# Revit family: SF_Tubest
name_source: partatom
category: Structural Framing
units: mm (PartAtom-declared; Revit-internal decimal feet)

## family parameters
Always export as geometry = No
Always vertical = Yes
Cut with Voids When Loaded = No
Material for Model Behavior = Other
OmniClass Number = 23.25.30.11.14.14
OmniClass Title = Beams
Section Shape = Not Defined
Shared = No
Show family pre-cut in plan views = Yes

## types (264) — shared parameters
A = 89 mm
D2_o = 18 mm
D2_s = 20 mm
D_o = 18 mm
D_s = 25 mm
Dse = 20 mm
Ro = 10 mm
Rs = 8 mm

## per-type parameters (varying)
| type | B | H | Offset_o | Offset_s | Vis.Sigma | Vis.SigmaEspecial | Y | eo | es |
| TubestGD (800x400x6x4 | 400 mm | 800 mm | 400 mm | 200 mm | Yes | No | 670 mm | 6 mm | 4 mm |
| TubestGD (800x400x6x3 | 400 mm | 800 mm | 400 mm | 200 mm | Yes | No | 670 mm | 6 mm | 3 mm |
| TubestGD (800x400x5x3 | 400 mm | 800 mm | 400 mm | 200 mm | Yes | No | 670 mm | 5 mm | 3 mm |
| TubestGD (800x400x4x3 | 400 mm | 800 mm | 400 mm | 200 mm | Yes | No | 670 mm | 4 mm | 3 mm |
| TubestGD (800x400x3x3 | 400 mm | 800 mm | 400 mm | 200 mm | Yes | No | 670 mm | 3 mm | 3 mm |
| TubestGD (800x350x6x4 | 350 mm | 800 mm | 400 mm | 175 mm | Yes | No | 670 mm | 6 mm | 4 mm |
| TubestGD (800x350x6x3 | 350 mm | 800 mm | 400 mm | 175 mm | Yes | No | 670 mm | 6 mm | 3 mm |
| TubestGD (800x350x5x3 | 350 mm | 800 mm | 400 mm | 175 mm | Yes | No | 670 mm | 5 mm | 3 mm |
| TubestGD (800x350x4x3 | 350 mm | 800 mm | 400 mm | 175 mm | Yes | No | 670 mm | 4 mm | 3 mm |
| TubestGD (800x350x3x3 | 350 mm | 800 mm | 400 mm | 175 mm | Yes | No | 670 mm | 3 mm | 3 mm |
| TubestGD (800x300x6x4 | 300 mm | 800 mm | 400 mm | 150 mm | Yes | No | 670 mm | 6 mm | 4 mm |
| TubestGD (800x300x6x3 | 300 mm | 800 mm | 400 mm | 150 mm | Yes | No | 670 mm | 6 mm | 3 mm |
| TubestGD (800x300x5x3 | 300 mm | 800 mm | 400 mm | 150 mm | Yes | No | 670 mm | 5 mm | 3 mm |
| TubestGD (800x300x4x3 | 300 mm | 800 mm | 400 mm | 150 mm | Yes | No | 670 mm | 4 mm | 3 mm |
| TubestGD (800x300x3x3 | 300 mm | 800 mm | 400 mm | 150 mm | Yes | No | 670 mm | 3 mm | 3 mm |
| TubestGD (800x250x6x4 | 250 mm | 800 mm | 400 mm | 125 mm | Yes | No | 670 mm | 6 mm | 4 mm |
| TubestGD (800x250x6x3 | 250 mm | 800 mm | 400 mm | 125 mm | Yes | No | 670 mm | 6 mm | 3 mm |
| TubestGD (800x250x5x3 | 250 mm | 800 mm | 400 mm | 125 mm | Yes | No | 670 mm | 5 mm | 3 mm |
| TubestGD (800x250x4x3 | 250 mm | 800 mm | 400 mm | 125 mm | Yes | No | 670 mm | 4 mm | 3 mm |
| TubestGD (800x250x3x3 | 250 mm | 800 mm | 400 mm | 125 mm | Yes | No | 670 mm | 3 mm | 3 mm |
| TubestGD (800x225x6x4 | 225 mm | 800 mm | 400 mm | 113 mm | Yes | No | 670 mm | 6 mm | 4 mm |
| TubestGD (800x225x6x3 | 225 mm | 800 mm | 400 mm | 113 mm | Yes | No | 670 mm | 6 mm | 3 mm |
| TubestGD (800x225x5x3 | 225 mm | 800 mm | 400 mm | 113 mm | Yes | No | 670 mm | 5 mm | 3 mm |
| TubestGD (800x225x4x3 | 225 mm | 800 mm | 400 mm | 113 mm | Yes | No | 670 mm | 4 mm | 3 mm |
| TubestGD (800x225x3x3 | 225 mm | 800 mm | 400 mm | 113 mm | Yes | No | 670 mm | 3 mm | 3 mm |
| TubestGD (800x200x6x4 | 200 mm | 800 mm | 400 mm | 100 mm | Yes | No | 670 mm | 6 mm | 4 mm |
| TubestGD (800x200x6x3 | 200 mm | 800 mm | 400 mm | 100 mm | Yes | No | 670 mm | 6 mm | 3 mm |
| TubestGD (800x200x5x3 | 200 mm | 800 mm | 400 mm | 100 mm | Yes | No | 670 mm | 5 mm | 3 mm |
| TubestGD (800x200x4x3 | 200 mm | 800 mm | 400 mm | 100 mm | Yes | No | 670 mm | 4 mm | 3 mm |
| TubestGD (800x200x3x3 | 200 mm | 800 mm | 400 mm | 100 mm | Yes | No | 670 mm | 3 mm | 3 mm |
| TubestGD (800x150x6x4 | 150 mm | 800 mm | 400 mm | 75 mm | Yes | No | 670 mm | 6 mm | 4 mm |
| TubestGD (800x150x6x3 | 150 mm | 800 mm | 400 mm | 75 mm | Yes | No | 670 mm | 6 mm | 3 mm |
| TubestGD (800x150x5x3 | 150 mm | 800 mm | 400 mm | 75 mm | Yes | No | 670 mm | 5 mm | 3 mm |
| TubestGD (800x150x4x3 | 150 mm | 800 mm | 400 mm | 75 mm | Yes | No | 670 mm | 4 mm | 3 mm |
| TubestGD (800x150x3x3 | 150 mm | 800 mm | 400 mm | 75 mm | Yes | No | 670 mm | 3 mm | 3 mm |
| TubestGD (750x400x6x4 | 400 mm | 750 mm | 375 mm | 200 mm | Yes | No | 620 mm | 6 mm | 4 mm |
| TubestGD (750x400x6x3 | 400 mm | 750 mm | 375 mm | 200 mm | Yes | No | 620 mm | 6 mm | 3 mm |
| TubestGD (750x400x5x3 | 400 mm | 750 mm | 375 mm | 200 mm | Yes | No | 620 mm | 5 mm | 3 mm |
| TubestGD (750x400x4x3 | 400 mm | 750 mm | 375 mm | 200 mm | Yes | No | 620 mm | 4 mm | 3 mm |
| TubestGD (750x400x3x3 | 400 mm | 750 mm | 375 mm | 200 mm | Yes | No | 620 mm | 3 mm | 3 mm |
| TubestGD (750x350x6x4 | 350 mm | 750 mm | 375 mm | 175 mm | Yes | No | 620 mm | 6 mm | 4 mm |
| TubestGD (750x350x6x3 | 350 mm | 750 mm | 375 mm | 175 mm | Yes | No | 620 mm | 6 mm | 3 mm |
| TubestGD (750x350x5x3 | 350 mm | 750 mm | 375 mm | 175 mm | Yes | No | 620 mm | 5 mm | 3 mm |
| TubestGD (750x350x4x3 | 350 mm | 750 mm | 375 mm | 175 mm | Yes | No | 620 mm | 4 mm | 3 mm |
| TubestGD (750x350x3x3 | 350 mm | 750 mm | 375 mm | 175 mm | Yes | No | 620 mm | 3 mm | 3 mm |
| TubestGD (750x300x6x4 | 300 mm | 750 mm | 375 mm | 150 mm | Yes | No | 620 mm | 6 mm | 4 mm |
| TubestGD (750x300x6x3 | 300 mm | 750 mm | 375 mm | 150 mm | Yes | No | 620 mm | 6 mm | 3 mm |
| TubestGD (750x300x5x3 | 300 mm | 750 mm | 375 mm | 150 mm | Yes | No | 620 mm | 5 mm | 3 mm |
| TubestGD (750x300x4x3 | 300 mm | 750 mm | 375 mm | 150 mm | Yes | No | 620 mm | 4 mm | 3 mm |
| TubestGD (750x300x3x3 | 300 mm | 750 mm | 375 mm | 150 mm | Yes | No | 620 mm | 3 mm | 3 mm |
| TubestGD (750x250x6x4 | 250 mm | 750 mm | 375 mm | 125 mm | Yes | No | 620 mm | 6 mm | 4 mm |
| TubestGD (750x250x6x3 | 250 mm | 750 mm | 375 mm | 125 mm | Yes | No | 620 mm | 6 mm | 3 mm |
| TubestGD (750x250x5x3 | 250 mm | 750 mm | 375 mm | 125 mm | Yes | No | 620 mm | 5 mm | 3 mm |
| TubestGD (750x250x4x3 | 250 mm | 750 mm | 375 mm | 125 mm | Yes | No | 620 mm | 4 mm | 3 mm |
| TubestGD (750x250x3x3 | 250 mm | 750 mm | 375 mm | 125 mm | Yes | No | 620 mm | 3 mm | 3 mm |
| TubestGD (750x225x6x4 | 225 mm | 750 mm | 375 mm | 113 mm | Yes | No | 620 mm | 6 mm | 4 mm |
| TubestGD (750x225x6x3 | 225 mm | 750 mm | 375 mm | 113 mm | Yes | No | 620 mm | 6 mm | 3 mm |
| TubestGD (750x225x5x3 | 225 mm | 750 mm | 375 mm | 113 mm | Yes | No | 620 mm | 5 mm | 3 mm |
| TubestGD (750x225x4x3 | 225 mm | 750 mm | 375 mm | 113 mm | Yes | No | 620 mm | 4 mm | 3 mm |
| TubestGD (750x225x3x3 | 225 mm | 750 mm | 375 mm | 113 mm | Yes | No | 620 mm | 3 mm | 3 mm |
| TubestGD (750x200x6x4 | 200 mm | 750 mm | 375 mm | 100 mm | Yes | No | 620 mm | 6 mm | 4 mm |
| TubestGD (750x200x6x3 | 200 mm | 750 mm | 375 mm | 100 mm | Yes | No | 620 mm | 6 mm | 3 mm |
| TubestGD (750x200x5x3 | 200 mm | 750 mm | 375 mm | 100 mm | Yes | No | 620 mm | 5 mm | 3 mm |
| TubestGD (750x200x4x3 | 200 mm | 750 mm | 375 mm | 100 mm | Yes | No | 620 mm | 4 mm | 3 mm |
| TubestGD (750x200x3x3 | 200 mm | 750 mm | 375 mm | 100 mm | Yes | No | 620 mm | 3 mm | 3 mm |
| TubestGD (750x150x6x4 | 150 mm | 750 mm | 375 mm | 75 mm | Yes | No | 620 mm | 6 mm | 4 mm |
| TubestGD (750x150x6x3 | 150 mm | 750 mm | 375 mm | 75 mm | Yes | No | 620 mm | 6 mm | 3 mm |
| TubestGD (750x150x5x3 | 150 mm | 750 mm | 375 mm | 75 mm | Yes | No | 620 mm | 5 mm | 3 mm |
| TubestGD (750x150x4x3 | 150 mm | 750 mm | 375 mm | 75 mm | Yes | No | 620 mm | 4 mm | 3 mm |
| TubestGD (750x150x3x3 | 150 mm | 750 mm | 375 mm | 75 mm | Yes | No | 620 mm | 3 mm | 3 mm |
| TubestGD (700x400x6x4 | 400 mm | 700 mm | 350 mm | 200 mm | Yes | No | 570 mm | 6 mm | 4 mm |
| TubestGD (700x400x6x3 | 400 mm | 700 mm | 350 mm | 200 mm | Yes | No | 570 mm | 6 mm | 3 mm |
| TubestGD (700x400x5x3 | 400 mm | 700 mm | 350 mm | 200 mm | Yes | No | 570 mm | 5 mm | 3 mm |
| TubestGD (700x400x4x3 | 400 mm | 700 mm | 350 mm | 200 mm | Yes | No | 570 mm | 4 mm | 3 mm |
| TubestGD (700x400x3x3 | 400 mm | 700 mm | 350 mm | 200 mm | Yes | No | 570 mm | 3 mm | 3 mm |
| TubestGD (700x350x6x4 | 350 mm | 700 mm | 350 mm | 175 mm | Yes | No | 570 mm | 6 mm | 4 mm |
| TubestGD (700x350x6x3 | 350 mm | 700 mm | 350 mm | 175 mm | Yes | No | 570 mm | 6 mm | 3 mm |
| TubestGD (700x350x5x3 | 350 mm | 700 mm | 350 mm | 175 mm | Yes | No | 570 mm | 5 mm | 3 mm |
| TubestGD (700x350x4x3 | 350 mm | 700 mm | 350 mm | 175 mm | Yes | No | 570 mm | 4 mm | 3 mm |
| TubestGD (700x350x3x3 | 350 mm | 700 mm | 350 mm | 175 mm | Yes | No | 570 mm | 3 mm | 3 mm |
| TubestGD (700x300x6x4 | 300 mm | 700 mm | 350 mm | 150 mm | Yes | No | 570 mm | 6 mm | 4 mm |
| TubestGD (700x300x6x3 | 300 mm | 700 mm | 350 mm | 150 mm | Yes | No | 570 mm | 6 mm | 3 mm |
| TubestGD (700x300x5x3 | 300 mm | 700 mm | 350 mm | 150 mm | Yes | No | 570 mm | 5 mm | 3 mm |
| TubestGD (700x300x4x3 | 300 mm | 700 mm | 350 mm | 150 mm | Yes | No | 570 mm | 4 mm | 3 mm |
| TubestGD (700x300x3x3 | 300 mm | 700 mm | 350 mm | 150 mm | Yes | No | 570 mm | 3 mm | 3 mm |
| TubestGD (700x250x6x4 | 250 mm | 700 mm | 350 mm | 125 mm | Yes | No | 570 mm | 6 mm | 4 mm |
| TubestGD (700x250x6x3 | 250 mm | 700 mm | 350 mm | 125 mm | Yes | No | 570 mm | 6 mm | 3 mm |
| TubestGD (700x250x5x3 | 250 mm | 700 mm | 350 mm | 125 mm | Yes | No | 570 mm | 5 mm | 3 mm |
| TubestGD (700x250x4x3 | 250 mm | 700 mm | 350 mm | 125 mm | Yes | No | 570 mm | 4 mm | 3 mm |
| TubestGD (700x250x3x3 | 250 mm | 700 mm | 350 mm | 125 mm | Yes | No | 570 mm | 3 mm | 3 mm |
| TubestGD (700x225x6x4 | 225 mm | 700 mm | 350 mm | 113 mm | Yes | No | 570 mm | 6 mm | 4 mm |
| TubestGD (700x225x6x3 | 225 mm | 700 mm | 350 mm | 113 mm | Yes | No | 570 mm | 6 mm | 3 mm |
| TubestGD (700x225x5x3 | 225 mm | 700 mm | 350 mm | 113 mm | Yes | No | 570 mm | 5 mm | 3 mm |
| TubestGD (700x225x4x3 | 225 mm | 700 mm | 350 mm | 113 mm | Yes | No | 570 mm | 4 mm | 3 mm |
| TubestGD (700x225x3x3 | 225 mm | 700 mm | 350 mm | 113 mm | Yes | No | 570 mm | 3 mm | 3 mm |
| TubestGD (700x200x6x4 | 200 mm | 700 mm | 350 mm | 100 mm | Yes | No | 570 mm | 6 mm | 4 mm |
| TubestGD (700x200x6x3 | 200 mm | 700 mm | 350 mm | 100 mm | Yes | No | 570 mm | 6 mm | 3 mm |
| TubestGD (700x200x5x3 | 200 mm | 700 mm | 350 mm | 100 mm | Yes | No | 570 mm | 5 mm | 3 mm |
| TubestGD (700x200x4x3 | 200 mm | 700 mm | 350 mm | 100 mm | Yes | No | 570 mm | 4 mm | 3 mm |
| TubestGD (700x200x3x3 | 200 mm | 700 mm | 350 mm | 100 mm | Yes | No | 570 mm | 3 mm | 3 mm |
| TubestGD (700x150x6x4 | 150 mm | 700 mm | 350 mm | 75 mm | Yes | No | 570 mm | 6 mm | 4 mm |
| TubestGD (700x150x6x3 | 150 mm | 700 mm | 350 mm | 75 mm | Yes | No | 570 mm | 6 mm | 3 mm |
| TubestGD (700x150x5x3 | 150 mm | 700 mm | 350 mm | 75 mm | Yes | No | 570 mm | 5 mm | 3 mm |
| TubestGD (700x150x4x3 | 150 mm | 700 mm | 350 mm | 75 mm | Yes | No | 570 mm | 4 mm | 3 mm |
| TubestGD (700x150x3x3 | 150 mm | 700 mm | 350 mm | 75 mm | Yes | No | 570 mm | 3 mm | 3 mm |
| TubestGD (650x400x6x4 | 400 mm | 650 mm | 325 mm | 200 mm | Yes | No | 520 mm | 6 mm | 4 mm |
| TubestGD (650x400x6x3 | 400 mm | 650 mm | 325 mm | 200 mm | Yes | No | 520 mm | 6 mm | 3 mm |
| TubestGD (650x400x5x3 | 400 mm | 650 mm | 325 mm | 200 mm | Yes | No | 520 mm | 5 mm | 3 mm |
| TubestGD (650x400x4x3 | 400 mm | 650 mm | 325 mm | 200 mm | Yes | No | 520 mm | 4 mm | 3 mm |
| TubestGD (650x400x3x3 | 400 mm | 650 mm | 325 mm | 200 mm | Yes | No | 520 mm | 3 mm | 3 mm |
| TubestGD (650x350x6x4 | 350 mm | 650 mm | 325 mm | 175 mm | Yes | No | 520 mm | 6 mm | 4 mm |
| TubestGD (650x350x6x3 | 350 mm | 650 mm | 325 mm | 175 mm | Yes | No | 520 mm | 6 mm | 3 mm |
| TubestGD (650x350x5x3 | 350 mm | 650 mm | 325 mm | 175 mm | Yes | No | 520 mm | 5 mm | 3 mm |
| TubestGD (650x350x4x3 | 350 mm | 650 mm | 325 mm | 175 mm | Yes | No | 520 mm | 4 mm | 3 mm |
| TubestGD (650x350x3x3 | 350 mm | 650 mm | 325 mm | 175 mm | Yes | No | 520 mm | 3 mm | 3 mm |
| TubestGD (650x300x6x4 | 300 mm | 650 mm | 325 mm | 150 mm | Yes | No | 520 mm | 6 mm | 4 mm |
| TubestGD (650x300x6x3 | 300 mm | 650 mm | 325 mm | 150 mm | Yes | No | 520 mm | 6 mm | 3 mm |
| TubestGD (650x300x5x3 | 300 mm | 650 mm | 325 mm | 150 mm | Yes | No | 520 mm | 5 mm | 3 mm |
| TubestGD (650x300x4x3 | 300 mm | 650 mm | 325 mm | 150 mm | Yes | No | 520 mm | 4 mm | 3 mm |
| TubestGD (650x300x3x3 | 300 mm | 650 mm | 325 mm | 150 mm | Yes | No | 520 mm | 3 mm | 3 mm |
| TubestGD (650x250x6x4 | 250 mm | 650 mm | 325 mm | 125 mm | Yes | No | 520 mm | 6 mm | 4 mm |
| TubestGD (650x250x6x3 | 250 mm | 650 mm | 325 mm | 125 mm | Yes | No | 520 mm | 6 mm | 3 mm |
| TubestGD (650x250x5x3 | 250 mm | 650 mm | 325 mm | 125 mm | Yes | No | 520 mm | 5 mm | 3 mm |
| TubestGD (650x250x4x3 | 250 mm | 650 mm | 325 mm | 125 mm | Yes | No | 520 mm | 4 mm | 3 mm |
| TubestGD (650x250x3x3 | 250 mm | 650 mm | 325 mm | 125 mm | Yes | No | 520 mm | 3 mm | 3 mm |
| TubestGD (650x225x6x4 | 225 mm | 650 mm | 325 mm | 113 mm | Yes | No | 520 mm | 6 mm | 4 mm |
| TubestGD (650x225x6x3 | 225 mm | 650 mm | 325 mm | 113 mm | Yes | No | 520 mm | 6 mm | 3 mm |
| TubestGD (650x225x5x3 | 225 mm | 650 mm | 325 mm | 113 mm | Yes | No | 520 mm | 5 mm | 3 mm |
| TubestGD (650x225x4x3 | 225 mm | 650 mm | 325 mm | 113 mm | Yes | No | 520 mm | 4 mm | 3 mm |
| TubestGD (650x225x3x3 | 225 mm | 650 mm | 325 mm | 113 mm | Yes | No | 520 mm | 3 mm | 3 mm |
| TubestGD (650x200x6x4 | 200 mm | 650 mm | 325 mm | 100 mm | Yes | No | 520 mm | 6 mm | 4 mm |
| TubestGD (650x200x6x3 | 200 mm | 650 mm | 325 mm | 100 mm | Yes | No | 520 mm | 6 mm | 3 mm |
| TubestGD (650x200x5x3 | 200 mm | 650 mm | 325 mm | 100 mm | Yes | No | 520 mm | 5 mm | 3 mm |
| TubestGD (650x200x4x3 | 200 mm | 650 mm | 325 mm | 100 mm | Yes | No | 520 mm | 4 mm | 3 mm |
| TubestGD (650x200x3x3 | 200 mm | 650 mm | 325 mm | 100 mm | Yes | No | 520 mm | 3 mm | 3 mm |
| TubestGD (650x150x6x4 | 150 mm | 650 mm | 325 mm | 75 mm | Yes | No | 520 mm | 6 mm | 4 mm |
| TubestGD (650x150x6x3 | 150 mm | 650 mm | 325 mm | 75 mm | Yes | No | 520 mm | 6 mm | 3 mm |
| TubestGD (650x150x5x3 | 150 mm | 650 mm | 325 mm | 75 mm | Yes | No | 520 mm | 5 mm | 3 mm |
| TubestGD (650x150x4x3 | 150 mm | 650 mm | 325 mm | 75 mm | Yes | No | 520 mm | 4 mm | 3 mm |
| TubestGD (650x150x3x3 | 150 mm | 650 mm | 325 mm | 75 mm | Yes | No | 520 mm | 3 mm | 3 mm |
| TubestGD (600x400x6x4 | 400 mm | 600 mm | 300 mm | 200 mm | Yes | No | 470 mm | 6 mm | 4 mm |
| TubestGD (600x400x6x3 | 400 mm | 600 mm | 300 mm | 200 mm | Yes | No | 470 mm | 6 mm | 3 mm |
| TubestGD (600x400x5x3 | 400 mm | 600 mm | 300 mm | 200 mm | Yes | No | 470 mm | 5 mm | 3 mm |
| TubestGD (600x400x4x3 | 400 mm | 600 mm | 300 mm | 200 mm | Yes | No | 470 mm | 4 mm | 3 mm |
| TubestGD (600x400x3x3 | 400 mm | 600 mm | 300 mm | 200 mm | Yes | No | 470 mm | 3 mm | 3 mm |
| TubestGD (600x350x6x4 | 350 mm | 600 mm | 300 mm | 175 mm | Yes | No | 470 mm | 6 mm | 4 mm |
| TubestGD (600x350x6x3 | 350 mm | 600 mm | 300 mm | 175 mm | Yes | No | 470 mm | 6 mm | 3 mm |
| TubestGD (600x350x5x3 | 350 mm | 600 mm | 300 mm | 175 mm | Yes | No | 470 mm | 5 mm | 3 mm |
| TubestGD (600x350x4x3 | 350 mm | 600 mm | 300 mm | 175 mm | Yes | No | 470 mm | 4 mm | 3 mm |
| TubestGD (600x350x3x3 | 350 mm | 600 mm | 300 mm | 175 mm | Yes | No | 470 mm | 3 mm | 3 mm |
| TubestGD (600x300x6x4 | 300 mm | 600 mm | 300 mm | 150 mm | Yes | No | 470 mm | 6 mm | 4 mm |
| TubestGD (600x300x6x3 | 300 mm | 600 mm | 300 mm | 150 mm | Yes | No | 470 mm | 6 mm | 3 mm |
| TubestGD (600x300x5x3 | 300 mm | 600 mm | 300 mm | 150 mm | Yes | No | 470 mm | 5 mm | 3 mm |
| TubestGD (600x300x4x3 | 300 mm | 600 mm | 300 mm | 150 mm | Yes | No | 470 mm | 4 mm | 3 mm |
| TubestGD (600x300x3x3 | 300 mm | 600 mm | 300 mm | 150 mm | Yes | No | 470 mm | 3 mm | 3 mm |
| TubestGD (600x250x6x4 | 250 mm | 600 mm | 300 mm | 125 mm | Yes | No | 470 mm | 6 mm | 4 mm |
| TubestGD (600x250x6x3 | 250 mm | 600 mm | 300 mm | 125 mm | Yes | No | 470 mm | 6 mm | 3 mm |
| TubestGD (600x250x5x3 | 250 mm | 600 mm | 300 mm | 125 mm | Yes | No | 470 mm | 5 mm | 3 mm |
| TubestGD (600x250x4x3 | 250 mm | 600 mm | 300 mm | 125 mm | Yes | No | 470 mm | 4 mm | 3 mm |
| TubestGD (600x250x3x3 | 250 mm | 600 mm | 300 mm | 125 mm | Yes | No | 470 mm | 3 mm | 3 mm |
| TubestGD (600x225x6x4 | 225 mm | 600 mm | 300 mm | 113 mm | Yes | No | 470 mm | 6 mm | 4 mm |
| TubestGD (600x225x6x3 | 225 mm | 600 mm | 300 mm | 113 mm | Yes | No | 470 mm | 6 mm | 3 mm |
| TubestGD (600x225x5x3 | 225 mm | 600 mm | 300 mm | 113 mm | Yes | No | 470 mm | 5 mm | 3 mm |
| TubestGD (600x225x4x3 | 225 mm | 600 mm | 300 mm | 113 mm | Yes | No | 470 mm | 4 mm | 3 mm |
| TubestGD (600x225x3x3 | 225 mm | 600 mm | 300 mm | 113 mm | Yes | No | 470 mm | 3 mm | 3 mm |
| TubestGD (600x200x6x4 | 200 mm | 600 mm | 300 mm | 100 mm | Yes | No | 470 mm | 6 mm | 4 mm |
| TubestGD (600x200x6x3 | 200 mm | 600 mm | 300 mm | 100 mm | Yes | No | 470 mm | 6 mm | 3 mm |
| TubestGD (600x200x5x3 | 200 mm | 600 mm | 300 mm | 100 mm | Yes | No | 470 mm | 5 mm | 3 mm |
| TubestGD (600x200x4x3 | 200 mm | 600 mm | 300 mm | 100 mm | Yes | No | 470 mm | 4 mm | 3 mm |
| TubestGD (600x200x3x3 | 200 mm | 600 mm | 300 mm | 100 mm | Yes | No | 470 mm | 3 mm | 3 mm |
| TubestGD (600x150x6x4 | 150 mm | 600 mm | 300 mm | 75 mm | Yes | No | 470 mm | 6 mm | 4 mm |
| TubestGD (600x150x6x3 | 150 mm | 600 mm | 300 mm | 75 mm | Yes | No | 470 mm | 6 mm | 3 mm |
| TubestGD (600x150x5x3 | 150 mm | 600 mm | 300 mm | 75 mm | Yes | No | 470 mm | 5 mm | 3 mm |
| TubestGD (600x150x4x3 | 150 mm | 600 mm | 300 mm | 75 mm | Yes | No | 470 mm | 4 mm | 3 mm |
| TubestGD (600x150x3x3 | 150 mm | 600 mm | 300 mm | 75 mm | Yes | No | 470 mm | 3 mm | 3 mm |
| TubestGD (550x400x6x4 | 400 mm | 550 mm | 275 mm | 200 mm | Yes | No | 420 mm | 6 mm | 4 mm |
| TubestGD (550x400x6x3 | 400 mm | 550 mm | 275 mm | 200 mm | Yes | No | 420 mm | 6 mm | 3 mm |
| TubestGD (550x400x5x3 | 400 mm | 550 mm | 275 mm | 200 mm | Yes | No | 420 mm | 5 mm | 3 mm |
| TubestGD (550x400x4x3 | 400 mm | 550 mm | 275 mm | 200 mm | Yes | No | 420 mm | 4 mm | 3 mm |
| TubestGD (550x400x3x3 | 400 mm | 550 mm | 275 mm | 200 mm | Yes | No | 420 mm | 3 mm | 3 mm |
| TubestGD (550x350x6x4 | 350 mm | 550 mm | 275 mm | 175 mm | Yes | No | 420 mm | 6 mm | 4 mm |
| TubestGD (550x350x6x3 | 350 mm | 550 mm | 275 mm | 175 mm | Yes | No | 420 mm | 6 mm | 3 mm |
| TubestGD (550x350x5x3 | 350 mm | 550 mm | 275 mm | 175 mm | Yes | No | 420 mm | 5 mm | 3 mm |
| TubestGD (550x350x4x3 | 350 mm | 550 mm | 275 mm | 175 mm | Yes | No | 420 mm | 4 mm | 3 mm |
| TubestGD (550x350x3x3 | 350 mm | 550 mm | 275 mm | 175 mm | Yes | No | 420 mm | 3 mm | 3 mm |
| TubestGD (550x300x6x4 | 300 mm | 550 mm | 275 mm | 150 mm | Yes | No | 420 mm | 6 mm | 4 mm |
| TubestGD (550x300x6x3 | 300 mm | 550 mm | 275 mm | 150 mm | Yes | No | 420 mm | 6 mm | 3 mm |
| TubestGD (550x300x5x3 | 300 mm | 550 mm | 275 mm | 150 mm | Yes | No | 420 mm | 5 mm | 3 mm |
| TubestGD (550x300x4x3 | 300 mm | 550 mm | 275 mm | 150 mm | Yes | No | 420 mm | 4 mm | 3 mm |
| TubestGD (550x300x3x3 | 300 mm | 550 mm | 275 mm | 150 mm | Yes | No | 420 mm | 3 mm | 3 mm |
| TubestGD (550x250x6x4 | 250 mm | 550 mm | 275 mm | 125 mm | Yes | No | 420 mm | 6 mm | 4 mm |
| TubestGD (550x250x6x3 | 250 mm | 550 mm | 275 mm | 125 mm | Yes | No | 420 mm | 6 mm | 3 mm |
| TubestGD (550x250x5x3 | 250 mm | 550 mm | 275 mm | 125 mm | Yes | No | 420 mm | 5 mm | 3 mm |
| TubestGD (550x250x4x3 | 250 mm | 550 mm | 275 mm | 125 mm | Yes | No | 420 mm | 4 mm | 3 mm |
| TubestGD (550x250x3x3 | 250 mm | 550 mm | 275 mm | 125 mm | Yes | No | 420 mm | 3 mm | 3 mm |
| TubestGD (550x225x6x4 | 225 mm | 550 mm | 275 mm | 113 mm | Yes | No | 420 mm | 6 mm | 4 mm |
| TubestGD (550x225x6x3 | 225 mm | 550 mm | 275 mm | 113 mm | Yes | No | 420 mm | 6 mm | 3 mm |
| TubestGD (550x225x5x3 | 225 mm | 550 mm | 275 mm | 113 mm | Yes | No | 420 mm | 5 mm | 3 mm |
| TubestGD (550x225x4x3 | 225 mm | 550 mm | 275 mm | 113 mm | Yes | No | 420 mm | 4 mm | 3 mm |
| TubestGD (550x225x3x3 | 225 mm | 550 mm | 275 mm | 113 mm | Yes | No | 420 mm | 3 mm | 3 mm |
| TubestGD (550x200x6x4 | 200 mm | 550 mm | 275 mm | 100 mm | Yes | No | 420 mm | 6 mm | 4 mm |
| TubestGD (550x200x6x3 | 200 mm | 550 mm | 275 mm | 100 mm | Yes | No | 420 mm | 6 mm | 3 mm |
| TubestGD (550x200x5x3 | 200 mm | 550 mm | 275 mm | 100 mm | Yes | No | 420 mm | 5 mm | 3 mm |
| TubestGD (550x200x4x3 | 200 mm | 550 mm | 275 mm | 100 mm | Yes | No | 420 mm | 4 mm | 3 mm |
| TubestGD (550x200x3x3 | 200 mm | 550 mm | 275 mm | 100 mm | Yes | No | 420 mm | 3 mm | 3 mm |
| TubestGD (550x150x6x4 | 150 mm | 550 mm | 275 mm | 75 mm | Yes | No | 420 mm | 6 mm | 4 mm |
| TubestGD (550x150x6x3 | 150 mm | 550 mm | 275 mm | 75 mm | Yes | No | 420 mm | 6 mm | 3 mm |
| TubestGD (550x150x5x3 | 150 mm | 550 mm | 275 mm | 75 mm | Yes | No | 420 mm | 5 mm | 3 mm |
| TubestGD (550x150x4x3 | 150 mm | 550 mm | 275 mm | 75 mm | Yes | No | 420 mm | 4 mm | 3 mm |
| TubestGD (550x150x3x3 | 150 mm | 550 mm | 275 mm | 75 mm | Yes | No | 420 mm | 3 mm | 3 mm |
| Tubest (500x225x6x3 | 225 mm | 500 mm | 250 mm | 113 mm | Yes | No | 370 mm | 6 mm | 3 mm |
| Tubest (500x225x5x3 | 225 mm | 500 mm | 250 mm | 113 mm | Yes | No | 370 mm | 5 mm | 3 mm |
| Tubest (500x225x4x3 | 225 mm | 500 mm | 250 mm | 113 mm | Yes | No | 370 mm | 4 mm | 3 mm |
| Tubest (500x200x6x3 | 200 mm | 500 mm | 250 mm | 100 mm | Yes | No | 370 mm | 6 mm | 3 mm |
| Tubest (500x200x5x3 | 200 mm | 500 mm | 250 mm | 100 mm | Yes | No | 370 mm | 5 mm | 3 mm |
| Tubest (500x200x4x3 | 200 mm | 500 mm | 250 mm | 100 mm | Yes | No | 370 mm | 4 mm | 3 mm |
| Tubest (500x150x6x3 | 150 mm | 500 mm | 250 mm | 75 mm | Yes | No | 370 mm | 6 mm | 3 mm |
| Tubest (500x150x5x3 | 150 mm | 500 mm | 250 mm | 75 mm | Yes | No | 370 mm | 5 mm | 3 mm |
| Tubest (500x150x4x3 | 150 mm | 500 mm | 250 mm | 75 mm | Yes | No | 370 mm | 4 mm | 3 mm |
| Tubest (450x225x6x3 | 225 mm | 450 mm | 225 mm | 113 mm | Yes | No | 320 mm | 6 mm | 3 mm |
| Tubest (450x225x5x3 | 225 mm | 450 mm | 225 mm | 113 mm | Yes | No | 320 mm | 5 mm | 3 mm |
| Tubest (450x225x4x3 | 225 mm | 450 mm | 225 mm | 113 mm | Yes | No | 320 mm | 4 mm | 3 mm |
| Tubest (450x200x6x3 | 200 mm | 450 mm | 225 mm | 100 mm | Yes | No | 320 mm | 6 mm | 3 mm |
| Tubest (450x200x5x3 | 200 mm | 450 mm | 225 mm | 100 mm | Yes | No | 320 mm | 5 mm | 3 mm |
| Tubest (450x200x4x3 | 200 mm | 450 mm | 225 mm | 100 mm | Yes | No | 320 mm | 4 mm | 3 mm |
| Tubest (450x150x6x3 | 150 mm | 450 mm | 225 mm | 75 mm | Yes | No | 320 mm | 6 mm | 3 mm |
| Tubest (450x150x5x3 | 150 mm | 450 mm | 225 mm | 75 mm | Yes | No | 320 mm | 5 mm | 3 mm |
| Tubest (450x150x4x3 | 150 mm | 450 mm | 225 mm | 75 mm | Yes | No | 320 mm | 4 mm | 3 mm |
| Tubest (400x225x6x3 | 225 mm | 400 mm | 200 mm | 113 mm | Yes | No | 270 mm | 6 mm | 3 mm |
| Tubest (400x225x5x3 | 225 mm | 400 mm | 200 mm | 113 mm | Yes | No | 270 mm | 5 mm | 3 mm |
| Tubest (400x225x4x3 | 225 mm | 400 mm | 200 mm | 113 mm | Yes | No | 270 mm | 4 mm | 3 mm |
| Tubest (400x200x6x3 | 200 mm | 400 mm | 200 mm | 100 mm | Yes | No | 270 mm | 6 mm | 3 mm |
| Tubest (400x200x5x3 | 200 mm | 400 mm | 200 mm | 100 mm | Yes | No | 270 mm | 5 mm | 3 mm |
| Tubest (400x200x4x3 | 200 mm | 400 mm | 200 mm | 100 mm | Yes | No | 270 mm | 4 mm | 3 mm |
| Tubest (400x150x6x3 | 150 mm | 400 mm | 200 mm | 75 mm | Yes | No | 270 mm | 6 mm | 3 mm |
| Tubest (400x150x5x3 | 150 mm | 400 mm | 200 mm | 75 mm | Yes | No | 270 mm | 5 mm | 3 mm |
| Tubest (400x150x4x3 | 150 mm | 400 mm | 200 mm | 75 mm | Yes | No | 270 mm | 4 mm | 3 mm |
| Tubest (350x225x6x3 | 225 mm | 350 mm | 175 mm | 113 mm | Yes | No | 220 mm | 6 mm | 3 mm |
| Tubest (350x225x5x3 | 225 mm | 350 mm | 175 mm | 113 mm | Yes | No | 220 mm | 5 mm | 3 mm |
| Tubest (350x225x4x3 | 225 mm | 350 mm | 175 mm | 113 mm | Yes | No | 220 mm | 4 mm | 3 mm |
| Tubest (350x200x6x3 | 200 mm | 350 mm | 175 mm | 100 mm | Yes | No | 220 mm | 6 mm | 3 mm |
| Tubest (350x200x5x3 | 200 mm | 350 mm | 175 mm | 100 mm | Yes | No | 220 mm | 5 mm | 3 mm |
| Tubest (350x200x4x3 | 200 mm | 350 mm | 175 mm | 100 mm | Yes | No | 220 mm | 4 mm | 3 mm |
| Tubest (350x150x6x3 | 150 mm | 350 mm | 175 mm | 75 mm | Yes | No | 220 mm | 6 mm | 3 mm |
| Tubest (350x150x5x3 | 150 mm | 350 mm | 175 mm | 75 mm | Yes | No | 220 mm | 5 mm | 3 mm |
| Tubest (350x150x4x3 | 150 mm | 350 mm | 175 mm | 75 mm | Yes | No | 220 mm | 4 mm | 3 mm |
| Tubest (300x225x6x3 | 225 mm | 300 mm | 150 mm | 113 mm | Yes | No | 170 mm | 6 mm | 3 mm |
| Tubest (300x225x5x3 | 225 mm | 300 mm | 150 mm | 113 mm | Yes | No | 170 mm | 5 mm | 3 mm |
| Tubest (300x225x4x3 | 225 mm | 300 mm | 150 mm | 113 mm | Yes | No | 170 mm | 4 mm | 3 mm |
| Tubest (300x200x6x3 | 200 mm | 300 mm | 150 mm | 100 mm | Yes | No | 170 mm | 6 mm | 3 mm |
| Tubest (300x200x5x3 | 200 mm | 300 mm | 150 mm | 100 mm | Yes | No | 170 mm | 5 mm | 3 mm |
| Tubest (300x200x4x3 | 200 mm | 300 mm | 150 mm | 100 mm | Yes | No | 170 mm | 4 mm | 3 mm |
| Tubest (300x150x6x3 | 150 mm | 300 mm | 150 mm | 75 mm | Yes | No | 170 mm | 6 mm | 3 mm |
| Tubest (300x150x5x3 | 150 mm | 300 mm | 150 mm | 75 mm | Yes | No | 170 mm | 5 mm | 3 mm |
| Tubest (300x150x4x3 | 150 mm | 300 mm | 150 mm | 75 mm | Yes | No | 170 mm | 4 mm | 3 mm |
| Tubest (250x225x6x3 | 225 mm | 250 mm | 125 mm | 113 mm | No | Yes | 120 mm | 6 mm | 3 mm |
| Tubest (250x225x5x3 | 225 mm | 250 mm | 125 mm | 113 mm | No | Yes | 120 mm | 5 mm | 3 mm |
| Tubest (250x225x4x3 | 225 mm | 250 mm | 125 mm | 113 mm | No | Yes | 120 mm | 4 mm | 3 mm |
| Tubest (250x200x6x3 | 200 mm | 250 mm | 125 mm | 100 mm | No | Yes | 120 mm | 6 mm | 3 mm |
| Tubest (250x200x5x3 | 200 mm | 250 mm | 125 mm | 100 mm | No | Yes | 120 mm | 5 mm | 3 mm |
| Tubest (250x200x4x3 | 200 mm | 250 mm | 125 mm | 100 mm | No | Yes | 120 mm | 4 mm | 3 mm |
| Tubest (250x150x6x3 | 150 mm | 250 mm | 125 mm | 75 mm | No | Yes | 120 mm | 6 mm | 3 mm |
| Tubest (250x150x5x3 | 150 mm | 250 mm | 125 mm | 75 mm | No | Yes | 120 mm | 5 mm | 3 mm |
| Tubest (250x150x4x3 | 150 mm | 250 mm | 125 mm | 75 mm | No | Yes | 120 mm | 4 mm | 3 mm |

## geometry (parser evidence)
native form markers: Blend x2, Sweep x3
no freeform markers — native parametric forms only
